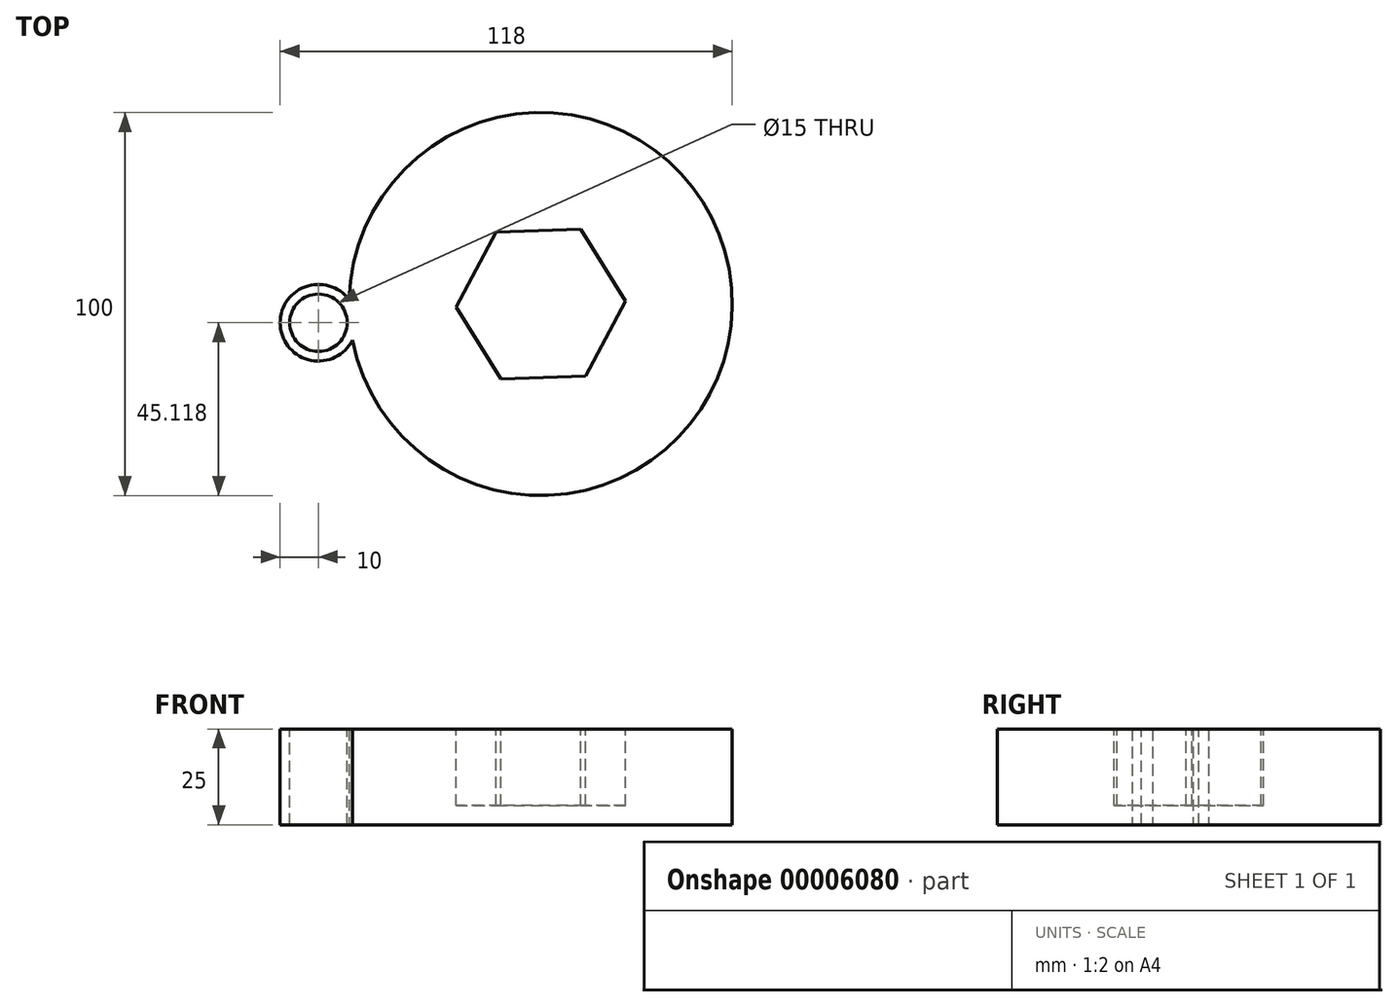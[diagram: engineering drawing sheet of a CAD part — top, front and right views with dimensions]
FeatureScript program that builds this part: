
annotation { "Feature Type Name" : "Feature", "Feature Type Description" : "" }
export const myFeature = defineFeature(function(context is Context, id is Id, definition is map)
    precondition{}
    {
        {
            var Q0;
            Q0=qCreatedBy(makeId("Right.planeOp"),FACE);
            var sketch = newSketch(context, id + "F0", { "sketchPlane" : qUnion([Q0])});
            skLineSegment(sketch, "E0.bottom", {"start": v(-20.02, -54.34) * mm, "end": v(9.98, -54.34) * mm});
            skLineSegment(sketch, "E0.top", {"start": v(-20.02, -24.34) * mm, "end": v(9.98, -24.34) * mm});
            skLineSegment(sketch, "E0.left", {"start": v(-20.02, -54.34) * mm, "end": v(-20.02, -24.34) * mm});
            skLineSegment(sketch, "E0.right", {"start": v(9.98, -54.34) * mm, "end": v(9.98, -24.34) * mm});
            skSolve(sketch);
        }
        {
            var Q0;
            Q0 = qSketchRegion(id + "F0", true);
            var Q1;
            Q1 = qSketchRegion(id + "FLX57TrYieNxJHR_1", true);
            extrude(context, id + "F1", {"entities" : qUnion([Q0, Q1]), "depth" : 30 * mm});
        }
        {
            var Q0;
            Q0=makeQuery(id+"F1.opExtrude","SWEPT_FACE",FACE,{"disambiguationData":[OSD([sQuery(id+"F0.wireOp",EDGE,"E0.left")])]});
            var sketch = newSketch(context, id + "F2", { "sketchPlane" : qUnion([Q0])});
            skCircle(sketch, "E1", {"center": v(15, -39.34) * mm, "radius": 7.5 * mm});
            skSolve(sketch);
        }
        {
            var Q0;
            Q0 = qSketchRegion(id + "F2", true);
            extrude(context, id + "F3", {"entities" : qUnion([Q0]), "operationType" : NewBodyOperationType.REMOVE, "endBound" : BoundingType.THROUGH_ALL, "oppositeDirection" : true, "depth" : 25 * mm});
        }
        {
            var Q0;
            Q0=makeQuery(id+"F1.opExtrude","SWEPT_FACE",FACE,{"disambiguationData":[OSD([sQuery(id+"F0.wireOp",EDGE,"E0.bottom")])]});
            var sketch = newSketch(context, id + "F4", { "sketchPlane" : qUnion([Q0])});
            skCircle(sketch, "E2.cCircle", {"center": v(12.5, 4.52) * mm, "radius": 4.5 * mm, "construction": true});
            skLineSegment(sketch, "E2.0", {"start": v(8, -3.27) * mm, "end": v(8, 12.32) * mm});
            skLineSegment(sketch, "E2.1", {"start": v(8, 12.32) * mm, "end": v(21.5, 4.52) * mm});
            skLineSegment(sketch, "E2.2", {"start": v(21.5, 4.52) * mm, "end": v(8, -3.27) * mm});
            skPoint(sketch, "E2.0.midPoint", {"position": v(8, 4.52) * mm});
            skSolve(sketch);
        }
        {
            var Q0;
            Q0 = qSketchRegion(id + "F4", true);
            extrude(context, id + "F5", {"entities" : qUnion([Q0]), "operationType" : NewBodyOperationType.REMOVE, "endBound" : BoundingType.THROUGH_ALL, "oppositeDirection" : true, "depth" : 25 * mm});
        }
        {
            var Q0;
            Q0=qCreatedBy(makeId("Top.planeOp"),FACE);
            var sketch = newSketch(context, id + "F6", { "sketchPlane" : qUnion([Q0])});
            skCircle(sketch, "E3", {"center": v(0, 0) * mm, "radius": 50 * mm});
            skCircle(sketch, "E4", {"center": v(-58, -4.88) * mm, "radius": 10 * mm});
            skSolve(sketch);
        }
        {
            var Q0;
            Q0=makeQuery(id+"F1.opExtrude","SWEPT_BODY",BODY,{"disambiguationData":[OSD([sQuery(id+"F0.wireOp",EDGE,"E0.bottom"),sQuery(id+"F0.wireOp",EDGE,"E0.top"),sQuery(id+"F0.wireOp",EDGE,"E0.left"),sQuery(id+"F0.wireOp",EDGE,"E0.right")])]});
            deleteBodies(context, id + "F7", {"entities" : qUnion([Q0])});
        }
        {
            var Q0;
            Q0 = qSketchRegion(id + "F6", true);
            extrude(context, id + "F8", {"entities" : qUnion([Q0]), "depth" : 25 * mm});
        }
        {
            var Q0;
            Q0=makeQuery(id+"F8.opExtrude","CAP_FACE",FACE,{"disambiguationData":[OSD([sQuery(id+"F6.wireOp",EDGE,"E3"),sQuery(id+"F6.wireOp",EDGE,"E4")])],"isStart":false});
            var sketch = newSketch(context, id + "F9", { "sketchPlane" : qUnion([Q0])});
            skCircle(sketch, "E5", {"center": v(-58, -4.88) * mm, "radius": 7.5 * mm});
            skSolve(sketch);
        }
        {
            var Q0;
            Q0 = qSketchRegion(id + "F9", true);
            extrude(context, id + "F10", {"entities" : qUnion([Q0]), "operationType" : NewBodyOperationType.REMOVE, "oppositeDirection" : true, "depth" : 25 * mm});
        }
        {
            var Q0;
            Q0=makeQuery(id+"F8.opExtrude","CAP_FACE",FACE,{"disambiguationData":[OSD([sQuery(id+"F6.wireOp",EDGE,"E3"),sQuery(id+"F6.wireOp",EDGE,"E4")])],"isStart":false});
            var sketch = newSketch(context, id + "F11", { "sketchPlane" : qUnion([Q0])});
            skCircle(sketch, "E6.cCircle", {"center": v(0, 0) * mm, "radius": 19.16 * mm, "construction": true});
            skLineSegment(sketch, "E6.0", {"start": v(22.11, 0.75) * mm, "end": v(11.7, -18.78) * mm});
            skLineSegment(sketch, "E6.1", {"start": v(11.7, -18.78) * mm, "end": v(-10.41, -19.52) * mm});
            skLineSegment(sketch, "E6.2", {"start": v(-10.41, -19.52) * mm, "end": v(-22.11, -0.75) * mm});
            skLineSegment(sketch, "E6.3", {"start": v(-22.11, -0.75) * mm, "end": v(-11.7, 18.78) * mm});
            skLineSegment(sketch, "E6.4", {"start": v(-11.7, 18.78) * mm, "end": v(10.41, 19.52) * mm});
            skLineSegment(sketch, "E6.5", {"start": v(10.41, 19.52) * mm, "end": v(22.11, 0.75) * mm});
            skPoint(sketch, "E6.0.midPoint", {"position": v(16.9, -9.02) * mm});
            skSolve(sketch);
        }
        {
            var Q0;
            Q0 = qSketchRegion(id + "F11", true);
            extrude(context, id + "F12", {"entities" : qUnion([Q0]), "operationType" : NewBodyOperationType.REMOVE, "oppositeDirection" : true, "depth" : 20 * mm});
        }
    });
